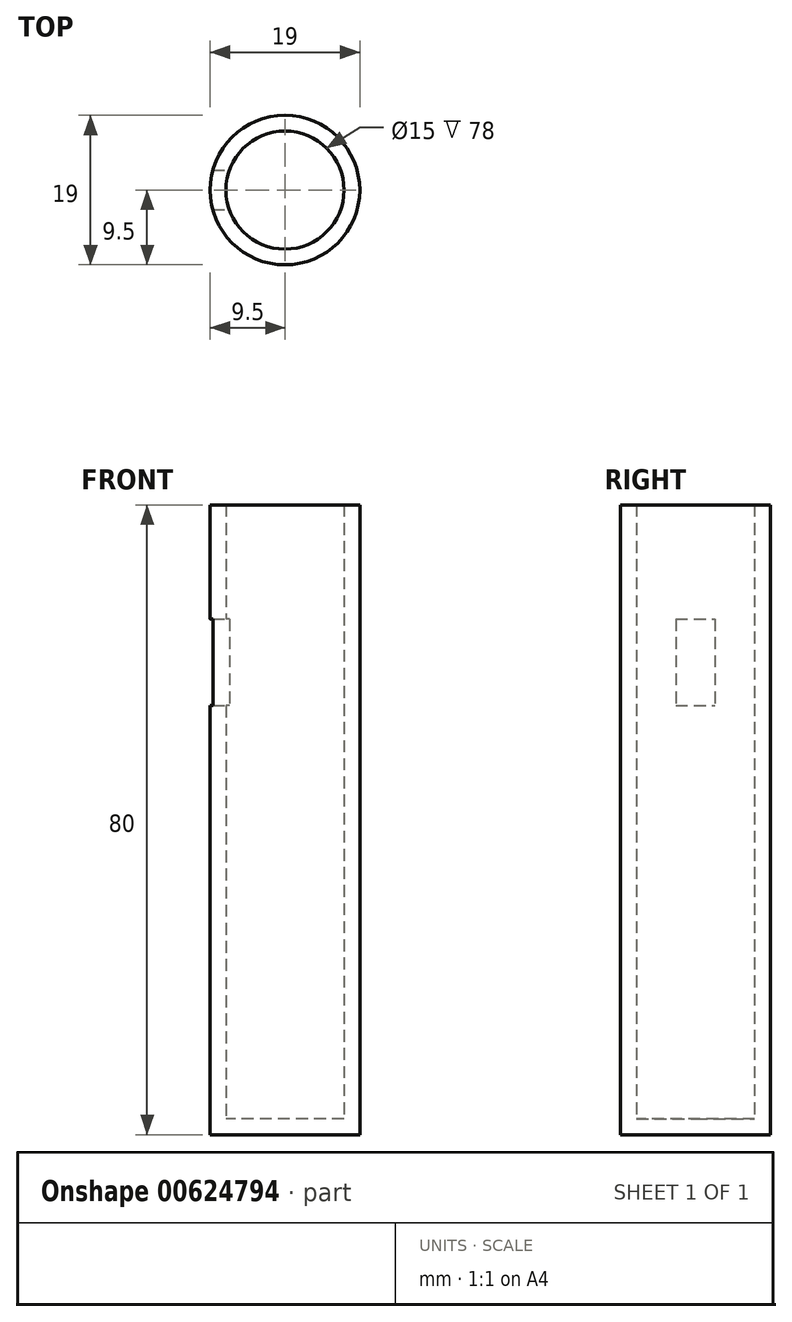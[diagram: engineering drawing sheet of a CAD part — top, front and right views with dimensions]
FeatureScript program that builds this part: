
annotation { "Feature Type Name" : "Feature", "Feature Type Description" : "" }
export const myFeature = defineFeature(function(context is Context, id is Id, definition is map)
    precondition{}
    {
        {
            var Q0;
            Q0=qCreatedBy(makeId("Top.planeOp"),FACE);
            var sketch = newSketch(context, id + "F0", { "sketchPlane" : qUnion([Q0])});
            skCircle(sketch, "E0", {"center": v(0, 0) * mm, "radius": 7.5 * mm});
            skCircle(sketch, "E1.0", {"center": v(0, 0) * mm, "radius": 9.5 * mm});
            skSolve(sketch);
        }
        {
            var Q0;
            Q0=makeQuery(id+"F0.imprint","IMPRINT",FACE,{"disambiguationData":[TD([[makeQuery(id+"F0.imprint","IMPRINT",EDGE,{"derivedFrom":sQuery(id+"F0.wireOp",EDGE,"E0")}),-1.0]])]});
            extrude(context, id + "F1", {"entities" : qUnion([Q0]), "depth" : 80 * mm, "offsetDistance" : 25 * mm});
        }
        {
            var Q0;
            Q0=qCreatedBy(makeId("Right.planeOp"),FACE);
            var sketch = newSketch(context, id + "F2", { "sketchPlane" : qUnion([Q0])});
            skLineSegment(sketch, "E2.bottom", {"start": v(-2.5, 65.5) * mm, "end": v(2.5, 65.5) * mm});
            skLineSegment(sketch, "E2.top", {"start": v(-2.5, 54.5) * mm, "end": v(2.5, 54.5) * mm});
            skLineSegment(sketch, "E2.left", {"start": v(-2.5, 65.5) * mm, "end": v(-2.5, 54.5) * mm});
            skLineSegment(sketch, "E2.right", {"start": v(2.5, 65.5) * mm, "end": v(2.5, 54.5) * mm});
            skLineSegment(sketch, "E3", {"start": v(-17, 60) * mm, "end": v(16.98, 60) * mm, "construction": true});
            skSolve(sketch);
        }
        {
            var Q0;
            Q0=qSketchRegion(id+"F2",true);
            extrude(context, id + "F3", {"entities" : qUnion([Q0]), "operationType" : NewBodyOperationType.REMOVE, "oppositeDirection" : true, "depth" : 25 * mm, "offsetDistance" : 25 * mm});
        }
        {
            var Q0;
            Q0=makeQuery(id+"F0.imprint","IMPRINT",FACE,{"disambiguationData":[TD([[makeQuery(id+"F0.imprint","IMPRINT",EDGE,{"derivedFrom":sQuery(id+"F0.wireOp",EDGE,"E0")}),1.0]])]});
            extrude(context, id + "F4", {"entities" : qUnion([Q0]), "operationType" : NewBodyOperationType.ADD, "depth" : 2 * mm, "offsetDistance" : 25 * mm});
        }
    });
